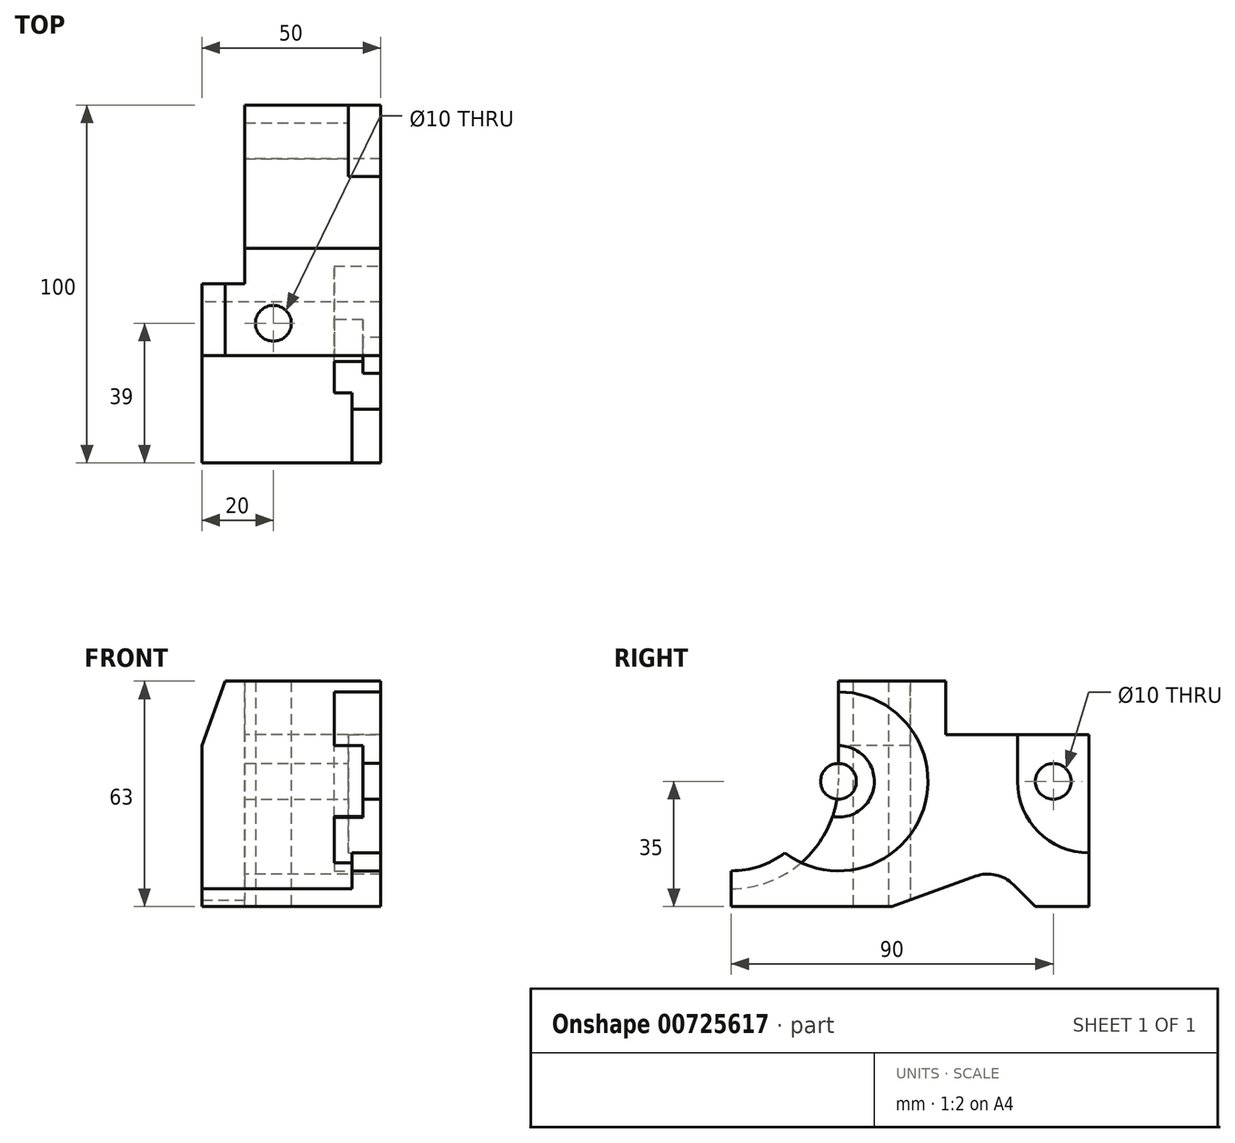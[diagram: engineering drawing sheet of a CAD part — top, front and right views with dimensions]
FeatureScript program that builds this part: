
annotation { "Feature Type Name" : "Feature", "Feature Type Description" : "" }
export const myFeature = defineFeature(function(context is Context, id is Id, definition is map)
    precondition{}
    {
        {
            var Q0;
            Q0=qCreatedBy(makeId("Right.planeOp"),FACE);
            var sketch = newSketch(context, id + "F0", { "sketchPlane" : qUnion([Q0])});
            skLineSegment(sketch, "E0", {"start": v(0, 0) * mm, "end": v(45, 0) * mm});
            skLineSegment(sketch, "E1", {"start": v(45, 0) * mm, "end": v(68.34, 8.5) * mm});
            skArc(sketch, "E2", {"start": v(68.34, 8.5) * mm, "mid": v(73.92, 8.86) * mm, "end": v(78.83, 6.17) * mm});
            skLineSegment(sketch, "E3", {"start": v(78.83, 6.17) * mm, "end": v(85, 0) * mm});
            skLineSegment(sketch, "E4", {"start": v(85, 0) * mm, "end": v(100, 0) * mm});
            skLineSegment(sketch, "E5", {"start": v(100, 0) * mm, "end": v(100, 48) * mm});
            skLineSegment(sketch, "E6", {"start": v(100, 48) * mm, "end": v(60, 48) * mm});
            skLineSegment(sketch, "E7", {"start": v(60, 48) * mm, "end": v(60, 63) * mm});
            skLineSegment(sketch, "E8", {"start": v(60, 63) * mm, "end": v(30, 63) * mm});
            skLineSegment(sketch, "E9", {"start": v(30, 63) * mm, "end": v(30, 35) * mm});
            skArc(sketch, "E10", {"start": v(30, 35) * mm, "mid": v(21.21, 13.79) * mm, "end": v(0, 5) * mm});
            skLineSegment(sketch, "E11", {"start": v(0, 5) * mm, "end": v(0, 0) * mm});
            skLineSegment(sketch, "E12", {"start": v(45, 0) * mm, "end": v(85, 0) * mm});
            skSolve(sketch);
        }
        {
            var Q0;
            Q0=makeQuery(id+"F0.imprint","IMPRINT",FACE,{"disambiguationData":[TD([[makeQuery(id+"F0.imprint","IMPRINT",EDGE,{"derivedFrom":sQuery(id+"F0.wireOp",EDGE,"E0")}),1.0]])]});
            extrude(context, id + "F1", {"entities" : qUnion([Q0]), "endBound" : BoundingType.SYMMETRIC, "depth" : 50 * mm, "offsetDistance" : 25 * mm});
        }
        {
            var Q0;
            Q0=makeQuery(id+"F1.opExtrude","CAP_FACE",FACE,{"disambiguationData":[OSD([sQuery(id+"F0.wireOp",EDGE,"E0"),sQuery(id+"F0.wireOp",EDGE,"E1"),sQuery(id+"F0.wireOp",EDGE,"E2"),sQuery(id+"F0.wireOp",EDGE,"E3"),sQuery(id+"F0.wireOp",EDGE,"E4"),sQuery(id+"F0.wireOp",EDGE,"E5"),sQuery(id+"F0.wireOp",EDGE,"E6"),sQuery(id+"F0.wireOp",EDGE,"E7"),sQuery(id+"F0.wireOp",EDGE,"E8"),sQuery(id+"F0.wireOp",EDGE,"E9"),sQuery(id+"F0.wireOp",EDGE,"E10"),sQuery(id+"F0.wireOp",EDGE,"E11")])],"isStart":false});
            var sketch = newSketch(context, id + "F2", { "sketchPlane" : qUnion([Q0])});
            skCircle(sketch, "E13", {"center": v(30, 35) * mm, "radius": 25 * mm});
            skSolve(sketch);
        }
        {
            var Q0;
            Q0 = qSketchRegion(id + "F2", true);
            extrude(context, id + "F3", {"entities" : qUnion([Q0]), "operationType" : NewBodyOperationType.REMOVE, "oppositeDirection" : true, "depth" : 13 * mm, "offsetDistance" : 25 * mm});
        }
        {
            var Q0;
            Q0=makeQuery(id+"F3.boolean.opBoolean","COPY",FACE,{"derivedFrom":makeQuery(id+"F3.opExtrude","CAP_FACE",FACE,{"disambiguationData":[OSD([sQuery(id+"F2.wireOp",EDGE,"E13")])],"isStart":false})});
            var sketch = newSketch(context, id + "F4", { "sketchPlane" : qUnion([Q0])});
            skArc(sketch, "E14", {"start": v(28.33, 25.14) * mm, "mid": v(39.96, 34.16) * mm, "end": v(30, 45) * mm});
            skLineSegment(sketch, "E15", {"start": v(30, 45) * mm, "end": v(30, 35) * mm});
            skArc(sketch, "E16", {"start": v(28.33, 25.14) * mm, "mid": v(29.58, 30) * mm, "end": v(30, 35) * mm});
            skSolve(sketch);
        }
        {
            var Q0;
            Q0 = qSketchRegion(id + "F4", true);
            extrude(context, id + "F5", {"entities" : qUnion([Q0]), "operationType" : NewBodyOperationType.ADD, "depth" : 8 * mm, "offsetDistance" : 25 * mm});
        }
        {
            var Q0;
            Q0=makeQuery(id+"F5.opExtrude","CAP_FACE",FACE,{"disambiguationData":[OSD([sQuery(id+"F4.wireOp",EDGE,"E14")])],"isStart":false});
            var sketch = newSketch(context, id + "F6", { "sketchPlane" : qUnion([Q0])});
            skCircle(sketch, "E17", {"center": v(30, 35) * mm, "radius": 5 * mm});
            skSolve(sketch);
        }
        {
            var Q0;
            Q0 = qSketchRegion(id + "F6", true);
            var Q1;
            Q1=makeQuery(id+"F1.opExtrude","CAP_FACE",FACE,{"disambiguationData":[OSD([sQuery(id+"F0.wireOp",EDGE,"E0"),sQuery(id+"F0.wireOp",EDGE,"E1"),sQuery(id+"F0.wireOp",EDGE,"E2"),sQuery(id+"F0.wireOp",EDGE,"E3"),sQuery(id+"F0.wireOp",EDGE,"E4"),sQuery(id+"F0.wireOp",EDGE,"E5"),sQuery(id+"F0.wireOp",EDGE,"E6"),sQuery(id+"F0.wireOp",EDGE,"E7"),sQuery(id+"F0.wireOp",EDGE,"E8"),sQuery(id+"F0.wireOp",EDGE,"E9"),sQuery(id+"F0.wireOp",EDGE,"E10"),sQuery(id+"F0.wireOp",EDGE,"E11")])],"isStart":false});
            extrude(context, id + "F7", {"entities" : qUnion([Q0]), "operationType" : NewBodyOperationType.ADD, "endBound" : BoundingType.UP_TO_SURFACE, "depth" : 5 * mm, "endBoundEntityFace" : qUnion([Q1]), "offsetDistance" : 25 * mm});
        }
        {
            var Q0;
            Q0=makeQuery(id+"F1.opExtrude","CAP_FACE",FACE,{"disambiguationData":[OSD([sQuery(id+"F0.wireOp",EDGE,"E0"),sQuery(id+"F0.wireOp",EDGE,"E1"),sQuery(id+"F0.wireOp",EDGE,"E2"),sQuery(id+"F0.wireOp",EDGE,"E3"),sQuery(id+"F0.wireOp",EDGE,"E4"),sQuery(id+"F0.wireOp",EDGE,"E5"),sQuery(id+"F0.wireOp",EDGE,"E6"),sQuery(id+"F0.wireOp",EDGE,"E7"),sQuery(id+"F0.wireOp",EDGE,"E8"),sQuery(id+"F0.wireOp",EDGE,"E9"),sQuery(id+"F0.wireOp",EDGE,"E10"),sQuery(id+"F0.wireOp",EDGE,"E11")])],"isStart":false});
            var sketch = newSketch(context, id + "F8", { "sketchPlane" : qUnion([Q0])});
            skLineSegment(sketch, "E18", {"start": v(0, 5) * mm, "end": v(0, 10) * mm});
            skArc(sketch, "E19", {"start": v(0, 10) * mm, "mid": v(7.9, 11.28) * mm, "end": v(15, 15) * mm});
            skArc(sketch, "E20", {"start": v(19.58, 12.27) * mm, "mid": v(17.22, 13.51) * mm, "end": v(15, 15) * mm});
            skSolve(sketch);
        }
        {
            var Q0;
            Q0=makeQuery(id+"F8.imprint","IMPRINT",FACE,{"disambiguationData":[TD([[makeQuery(id+"F8.imprint","IMPRINT",EDGE,{"derivedFrom":sQuery(id+"F8.wireOp",EDGE,"E18")}),-1.0]])]});
            extrude(context, id + "F9", {"entities" : qUnion([Q0]), "operationType" : NewBodyOperationType.ADD, "oppositeDirection" : true, "depth" : 8 * mm, "offsetDistance" : 25 * mm});
        }
        {
            var Q0;
            {var subQ0=sQuery(id+"F0.wireOp",EDGE,"E10");Q0=makeQuery(id+"F9.boolean.opBoolean","MERGE",FACE,{"derivedFrom":[makeQuery(id+"F1.opExtrude","CAP_FACE",FACE,{"disambiguationData":[OSD([sQuery(id+"F0.wireOp",EDGE,"E0"),sQuery(id+"F0.wireOp",EDGE,"E1"),sQuery(id+"F0.wireOp",EDGE,"E2"),sQuery(id+"F0.wireOp",EDGE,"E3"),sQuery(id+"F0.wireOp",EDGE,"E4"),sQuery(id+"F0.wireOp",EDGE,"E5"),sQuery(id+"F0.wireOp",EDGE,"E6"),sQuery(id+"F0.wireOp",EDGE,"E7"),sQuery(id+"F0.wireOp",EDGE,"E8"),sQuery(id+"F0.wireOp",EDGE,"E9"),subQ0,sQuery(id+"F0.wireOp",EDGE,"E11")])],"isStart":false}),makeQuery(id+"F9.opExtrude","CAP_FACE",FACE,{"disambiguationData":[OSD([subQ0,sQuery(id+"F8.wireOp",EDGE,"E18"),sQuery(id+"F8.wireOp",EDGE,"E19"),sQuery(id+"F8.wireOp",EDGE,"E20")])],"isStart":true})]});}
            var sketch = newSketch(context, id + "F10", { "sketchPlane" : qUnion([Q0])});
            skLineSegment(sketch, "E21", {"start": v(80, 48) * mm, "end": v(80, 35) * mm});
            skArc(sketch, "E22", {"start": v(80, 35) * mm, "mid": v(85.86, 20.86) * mm, "end": v(100, 15) * mm});
            skSolve(sketch);
        }
        {
            var Q0;
            {var subQ0=sQuery(id+"F10.wireOp",EDGE,"E21");Q0=makeQuery(id+"F10.imprint","IMPRINT",FACE,{"disambiguationData":[TD([[makeQuery(id+"F10.imprint","IMPRINT",EDGE,{"derivedFrom":subQ0}),1.0]])]});}
            extrude(context, id + "F11", {"entities" : qUnion([Q0]), "operationType" : NewBodyOperationType.REMOVE, "oppositeDirection" : true, "depth" : 9 * mm, "offsetDistance" : 25 * mm});
        }
        {
            var Q0;
            Q0=makeQuery(id+"F11.boolean.opBoolean","COPY",FACE,{"derivedFrom":makeQuery(id+"F11.opExtrude","CAP_FACE",FACE,{"disambiguationData":[OSD([sQuery(id+"F0.wireOp",EDGE,"E5"),sQuery(id+"F0.wireOp",EDGE,"E6"),sQuery(id+"F10.wireOp",EDGE,"E21"),sQuery(id+"F10.wireOp",EDGE,"E22")])],"isStart":false})});
            var sketch = newSketch(context, id + "F12", { "sketchPlane" : qUnion([Q0])});
            skCircle(sketch, "E23", {"center": v(90, 35) * mm, "radius": 5 * mm});
            skSolve(sketch);
        }
        {
            var Q0;
            Q0 = qSketchRegion(id + "F12", true);
            extrude(context, id + "F13", {"entities" : qUnion([Q0]), "operationType" : NewBodyOperationType.REMOVE, "endBound" : BoundingType.THROUGH_ALL, "oppositeDirection" : true, "depth" : 25 * mm, "offsetDistance" : 25 * mm});
        }
        {
            var Q0;
            Q0=makeQuery(id+"F1.opExtrude","SWEPT_FACE",FACE,{"disambiguationData":[OSD([sQuery(id+"F0.wireOp",EDGE,"E6")])]});
            var sketch = newSketch(context, id + "F14", { "sketchPlane" : qUnion([Q0])});
            skLineSegment(sketch, "E24.bottom", {"start": v(-25, 100) * mm, "end": v(-13, 100) * mm});
            skLineSegment(sketch, "E24.top", {"start": v(-25, 50) * mm, "end": v(-13, 50) * mm});
            skLineSegment(sketch, "E24.left", {"start": v(-25, 100) * mm, "end": v(-25, 50) * mm});
            skLineSegment(sketch, "E24.right", {"start": v(-13, 100) * mm, "end": v(-13, 50) * mm});
            skCircle(sketch, "E25", {"center": v(-5, 39) * mm, "radius": 5 * mm});
            skSolve(sketch);
        }
        {
            var Q0;
            Q0 = qSketchRegion(id + "F14", true);
            var Q1;
            Q1=sQuery(id+"F14.wireOp",EDGE,"E25");
            extrude(context, id + "F15", {"entities" : qUnion([Q0]), "operationType" : NewBodyOperationType.REMOVE, "surfaceEntities" : qUnion([Q1]), "endBound" : BoundingType.THROUGH_ALL, "depth" : 25 * mm, "offsetDistance" : 25 * mm});
        }
        {
            var Q0;
            Q0 = qSketchRegion(id + "F14", true);
            extrude(context, id + "F16", {"entities" : qUnion([Q0]), "operationType" : NewBodyOperationType.REMOVE, "endBound" : BoundingType.THROUGH_ALL, "oppositeDirection" : true, "depth" : 25 * mm, "offsetDistance" : 25 * mm});
        }
        {
            var Q0;
            Q0=makeQuery(id+"F5.boolean.opBoolean","MERGE",FACE,{"derivedFrom":[makeQuery(id+"F1.opExtrude","SWEPT_FACE",FACE,{"disambiguationData":[OSD([sQuery(id+"F0.wireOp",EDGE,"E9")])]}),makeQuery(id+"F5.opExtrude","SWEPT_FACE",FACE,{"disambiguationData":[OSD([sQuery(id+"F4.wireOp",EDGE,"E15")])]})]});
            var sketch = newSketch(context, id + "F17", { "sketchPlane" : qUnion([Q0])});
            skLineSegment(sketch, "E26", {"start": v(-18.45, 63) * mm, "end": v(-25, 45) * mm});
            skLineSegment(sketch, "E27", {"start": v(-25, 45) * mm, "end": v(-25, 63) * mm});
            skLineSegment(sketch, "E28", {"start": v(-25, 63) * mm, "end": v(-18.45, 63) * mm});
            skSolve(sketch);
        }
        {
            var Q0;
            Q0 = qSketchRegion(id + "F17", true);
            extrude(context, id + "F18", {"entities" : qUnion([Q0]), "operationType" : NewBodyOperationType.REMOVE, "endBound" : BoundingType.THROUGH_ALL, "oppositeDirection" : true, "depth" : 25 * mm, "offsetDistance" : 25 * mm});
        }
    });
